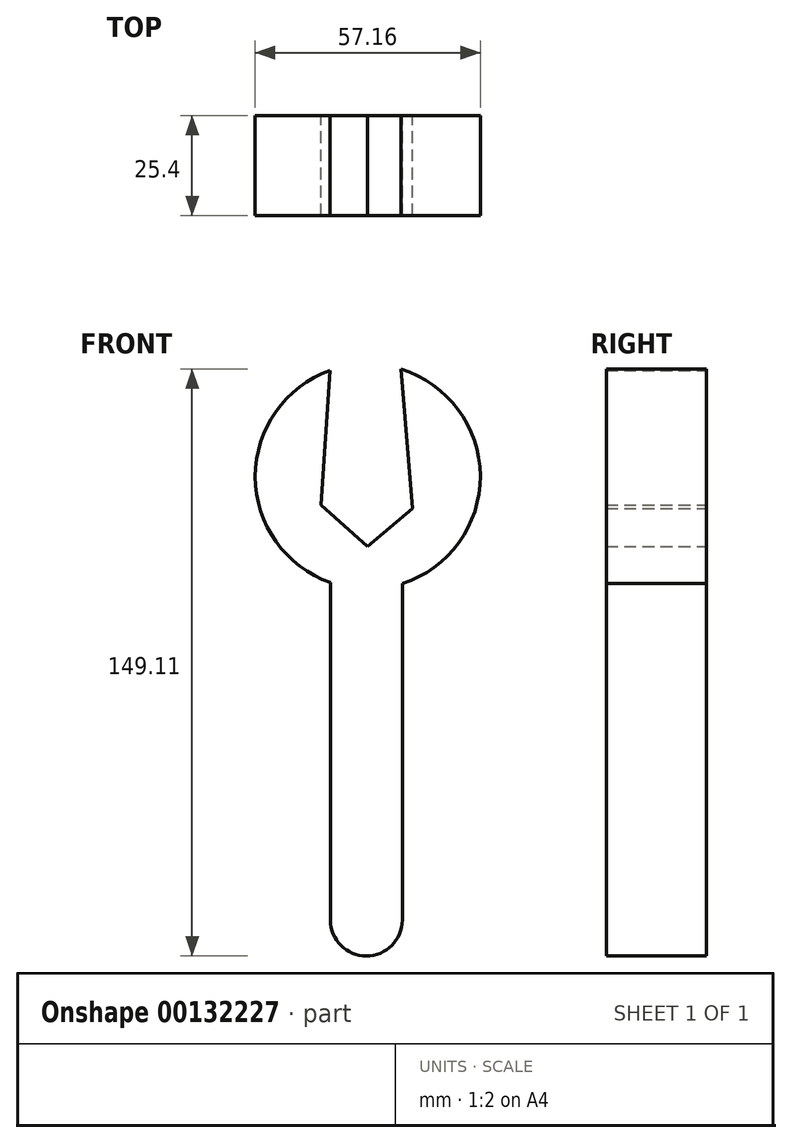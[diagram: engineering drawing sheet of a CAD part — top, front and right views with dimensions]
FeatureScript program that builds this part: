
annotation { "Feature Type Name" : "Feature", "Feature Type Description" : "" }
export const myFeature = defineFeature(function(context is Context, id is Id, definition is map)
    precondition{}
    {
        {
            var Q0;
            Q0=qCreatedBy(makeId("Front.planeOp"),FACE);
            var sketch = newSketch(context, id + "F0", { "sketchPlane" : qUnion([Q0])});
            skCircle(sketch, "E0", {"center": v(0, 48.35) * mm, "radius": 28.58 * mm});
            skLineSegment(sketch, "E1", {"start": v(-9.48, 21.4) * mm, "end": v(-9.48, -64.33) * mm});
            skLineSegment(sketch, "E2", {"start": v(8.78, 21.15) * mm, "end": v(8.78, -64.33) * mm});
            skArc(sketch, "E3", {"start": v(-9.48, -64.33) * mm, "mid": v(-0.35, -73.45) * mm, "end": v(8.78, -64.33) * mm});
            skLineSegment(sketch, "E4", {"start": v(-9.55, 75.3) * mm, "end": v(-11.9, 41.1) * mm});
            skLineSegment(sketch, "E5", {"start": v(-11.9, 41.1) * mm, "end": v(0, 30.64) * mm});
            skLineSegment(sketch, "E6", {"start": v(0, 30.64) * mm, "end": v(11.33, 40.22) * mm});
            skLineSegment(sketch, "E7", {"start": v(11.33, 40.22) * mm, "end": v(8.45, 75.66) * mm});
            skSolve(sketch);
        }
        {
            var Q0;
            {var subQ0=sQuery(id+"F0.wireOp",EDGE,"E4");Q0=makeQuery(id+"F0.imprint","IMPRINT",FACE,{"disambiguationData":[TD([[makeQuery(id+"F0.imprint","IMPRINT",EDGE,{"derivedFrom":subQ0}),-1.0]])]});}
            var Q1;
            {var subQ0=sQuery(id+"F0.wireOp",EDGE,"E1");Q1=makeQuery(id+"F0.imprint","IMPRINT",FACE,{"disambiguationData":[TD([[makeQuery(id+"F0.imprint","IMPRINT",EDGE,{"derivedFrom":subQ0}),1.0]])]});}
            extrude(context, id + "F1", {"entities" : qUnion([Q0, Q1]), "depth" : 25.4 * mm});
        }
    });
